# Revit family: Plumbing_Joints_Aignep_Condensed-Drain-Valve-Nptf-90976
name_source: partatom
category: Pipe Accessories
revit_build: Autodesk Revit 2018 (Build: 20170223_1515(x64)
units: mm (PartAtom-declared; Revit-internal decimal feet)

## family parameters
Always vertical = Yes
Cut with Voids When Loaded = No
OmniClass Number = 23.27.43.00
OmniClass Title = Pipe Fittings
Part Type = Valve - Breaks Into
Round Connector Dimension = Use Diameter
Shared = No
Work Plane-Based = No

## types (2) — shared parameters
A2 = 12.7 mm  [stored 0.0416667 ft]
Assembly Code = D2040100
BIMobject category = Valves
C = 12 mm  [stored 0.0393701 ft]
CH1 = 27 mm
CH2 = 25 mm  [stored 0.082021 ft]
CH3 = 16 mm
D = 13 mm
Description = Condensed drain valve NPTF
Design country = Italy
E = 65.5 mm
ES1 = 22 mm  [stored 0.0721785 ft]
ES2 = 23 mm
Edition number = 1
G = 26.5 mm
IFC Classification = Pipe Fitting
Keynote = 15410
Manufacturer = Aignep Spa
Manufacturer country = Italy
Manufacturer name = Aignep Spa
Material main = Brass
Model = 90976
Nominal Diameter 02 = 12.700 mm
OmniClass Code = 23-27 43 00
OmniClass Description = Pipe Fittings
Product Guid = a619ee7e-faa2-4660-8244-decc4a47eb16
Product Material = AIGNEP - Brass - Yellow
Product SKU = Condensed-Drain-Valve-Nptf-90976
Product certification = https://www.aignep.com
Product data url = https://www.bimobject.com
Product family = INFINITY
Product group = Valves
Product name = Condensed Drain Valve Nptf - 90976
Product url = https://www.aignep.com
QR code = https://www.bimobject.com
Tick Size 02 = 10.16 mm  [stored 0.0333333 ft]
URL = https://www.aignep.com

## per-type parameters (varying)
| type | A1 | B | L | Nominal Diameter 01 | OD | Tick Size 01 |
| D 3/8" | 9.525 mm  [stored 0.03125 ft] | 11.5 mm  [stored 0.0377297 ft] | 113.5 mm  [stored 0.372375 ft] | 9.525 mm | 17 mm | 7.62 mm  [stored 0.025 ft] |
| D 1/2" | 12.7 mm  [stored 0.0416667 ft] | 16 mm | 117.5 mm | 12.700 mm | 21.5 mm | 10.16 mm  [stored 0.0333333 ft] |

note: [stored X ft] marks values corroborated as IEEE doubles in the binary element streams (Revit-internal decimal feet)

## geometry (parser evidence)
native form markers: Sweep x2
no freeform markers — native parametric forms only
